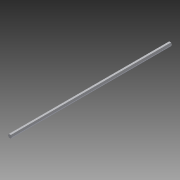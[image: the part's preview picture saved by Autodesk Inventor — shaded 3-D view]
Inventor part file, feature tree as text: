
AUTODESK INVENTOR PART (.ipt)
format: ipt  version: 2014 (Build 180170000, 170)  size: 71,168 bytes
history: native  units: in
note: dims shown in document units (in); Inventor stores cm internally (conversion verified against a paired STEP export)
features: extrude x1, sketch x1
ambient origin geometry x8: Origin, YZ Plane, XZ Plane, XY Plane, X Axis, Y Axis, Z Axis, Center Point
bodies: Solid1 (feature_tree)
feature tree (2):
  extrude  "Extrusion1"  Depth=25.0in TaperAngle=0.0deg
  sketch  "Sketch1"  dims[d0=0.5in d1=25.0in d2=0.0in]
